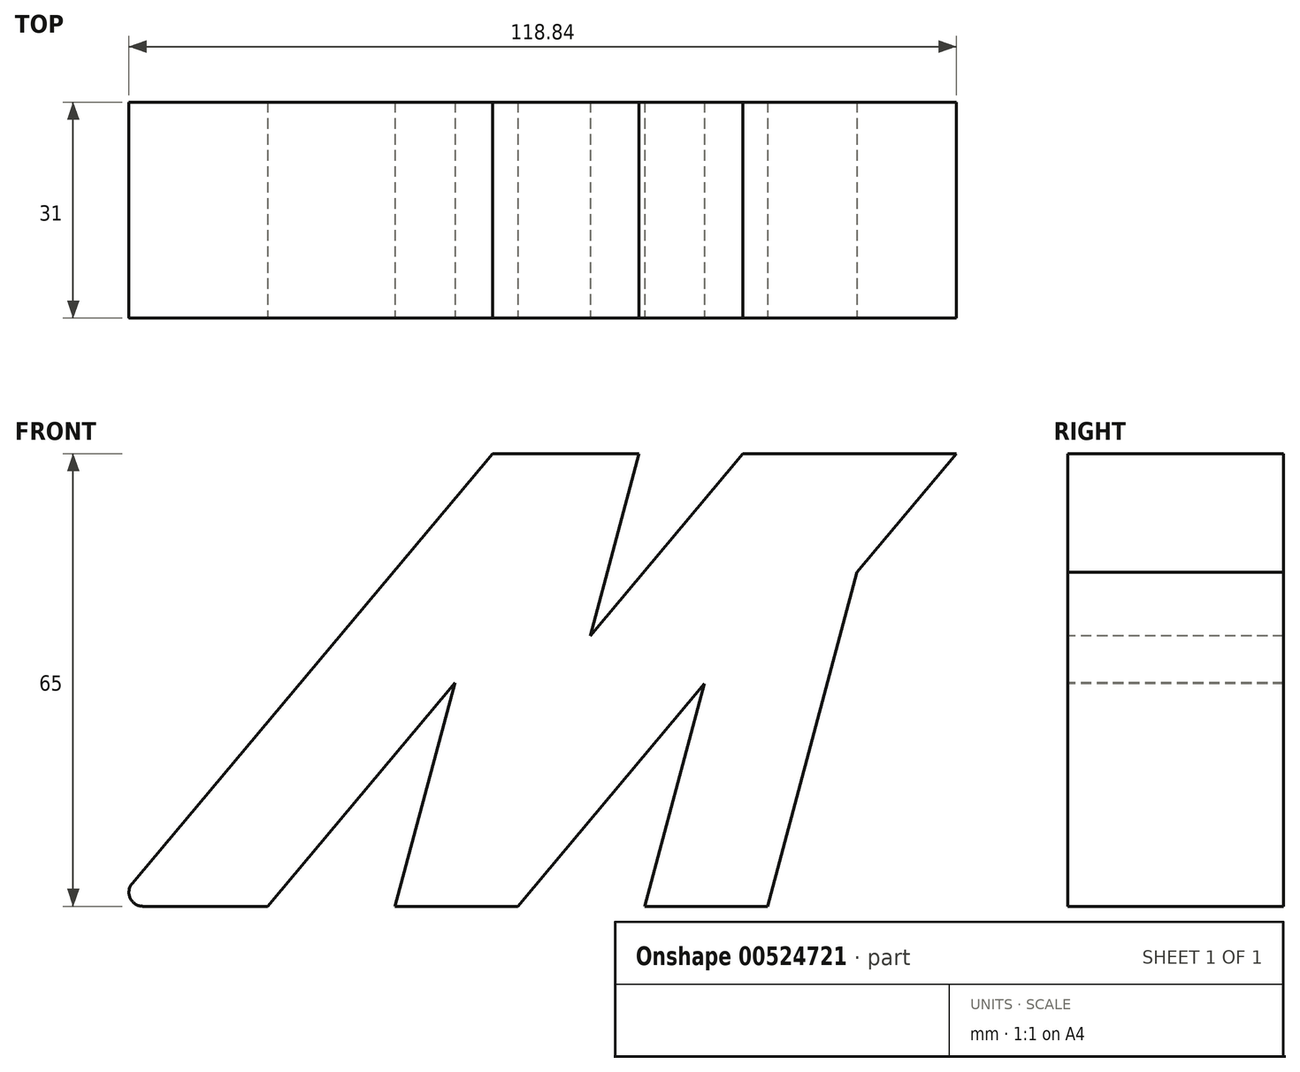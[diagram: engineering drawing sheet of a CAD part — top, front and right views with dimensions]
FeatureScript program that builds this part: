
annotation { "Feature Type Name" : "Feature", "Feature Type Description" : "" }
export const myFeature = defineFeature(function(context is Context, id is Id, definition is map)
    precondition{}
    {
        {
            var Q0;
            Q0=qCreatedBy(makeId("Front.planeOp"),FACE);
            var sketch = newSketch(context, id + "F0", { "sketchPlane" : qUnion([Q0])});
            skLineSegment(sketch, "E0", {"start": v(-72.25, -21.36) * mm, "end": v(-20.47, 40.35) * mm});
            skLineSegment(sketch, "E1", {"start": v(-20.47, 40.35) * mm, "end": v(0.53, 40.35) * mm});
            skLineSegment(sketch, "E2", {"start": v(0.53, 40.35) * mm, "end": v(-6.47, 14.2) * mm});
            skLineSegment(sketch, "E3", {"start": v(-6.47, 14.2) * mm, "end": v(15.46, 40.35) * mm});
            skLineSegment(sketch, "E4", {"start": v(15.46, 40.35) * mm, "end": v(46.12, 40.35) * mm});
            skLineSegment(sketch, "E5", {"start": v(46.12, 40.35) * mm, "end": v(31.85, 23.35) * mm});
            skLineSegment(sketch, "E6", {"start": v(31.85, 23.35) * mm, "end": v(19, -24.65) * mm});
            skLineSegment(sketch, "E7", {"start": v(19, -24.65) * mm, "end": v(1.4, -24.65) * mm});
            skLineSegment(sketch, "E8", {"start": v(1.4, -24.65) * mm, "end": v(9.96, 7.35) * mm});
            skLineSegment(sketch, "E9", {"start": v(9.96, 7.35) * mm, "end": v(-16.89, -24.65) * mm});
            skLineSegment(sketch, "E10", {"start": v(-16.89, -24.65) * mm, "end": v(-34.48, -24.65) * mm});
            skLineSegment(sketch, "E11", {"start": v(-34.48, -24.65) * mm, "end": v(-25.88, 7.45) * mm});
            skLineSegment(sketch, "E12", {"start": v(-25.88, 7.45) * mm, "end": v(-52.82, -24.65) * mm});
            skLineSegment(sketch, "E13", {"start": v(-52.82, -24.65) * mm, "end": v(-70.72, -24.65) * mm});
            skPoint(sketch, "E14.visualSharp", {"position": v(-75, -24.65) * mm});
            skArc(sketch, "E14.filletArc", {"start": v(-72.25, -21.36) * mm, "mid": v(-72.53, -23.5) * mm, "end": v(-70.72, -24.65) * mm});
            skSolve(sketch);
        }
        {
            var Q0;
            Q0=makeQuery(id+"F0.imprint","IMPRINT",FACE,{"disambiguationData":[TD([[makeQuery(id+"F0.imprint","IMPRINT",EDGE,{"derivedFrom":sQuery(id+"F0.wireOp",EDGE,"E0")}),-1.0]])]});
            var Q1;
            Q1=sQuery(id+"F0.wireOp",EDGE,"E13");
            var Q2;
            Q2=sQuery(id+"F0.wireOp",EDGE,"E0");
            var Q3;
            Q3=sQuery(id+"F0.wireOp",EDGE,"E1");
            var Q4;
            Q4=sQuery(id+"F0.wireOp",EDGE,"E2");
            var Q5;
            Q5=sQuery(id+"F0.wireOp",EDGE,"E3");
            var Q6;
            Q6=sQuery(id+"F0.wireOp",EDGE,"E4");
            var Q7;
            Q7=sQuery(id+"F0.wireOp",EDGE,"E5");
            var Q8;
            Q8=sQuery(id+"F0.wireOp",EDGE,"E6");
            var Q9;
            Q9=sQuery(id+"F0.wireOp",EDGE,"E7");
            var Q10;
            Q10=sQuery(id+"F0.wireOp",EDGE,"E8");
            var Q11;
            Q11=sQuery(id+"F0.wireOp",EDGE,"E9");
            var Q12;
            Q12=sQuery(id+"F0.wireOp",EDGE,"E10");
            var Q13;
            Q13=sQuery(id+"F0.wireOp",EDGE,"E11");
            var Q14;
            Q14=sQuery(id+"F0.wireOp",EDGE,"E12");
            var Q15;
            Q15=sQuery(id+"F0.wireOp",EDGE,"E14.filletArc");
            extrude(context, id + "F1", {"entities" : qUnion([Q0]), "bodyType" : ToolBodyType.SURFACE, "surfaceEntities" : qUnion([Q1, Q2, Q3, Q4, Q5, Q6, Q7, Q8, Q9, Q10, Q11, Q12, Q13, Q14, Q15]), "depth" : 31 * mm, "offsetDistance" : 25 * mm});
        }
    });
